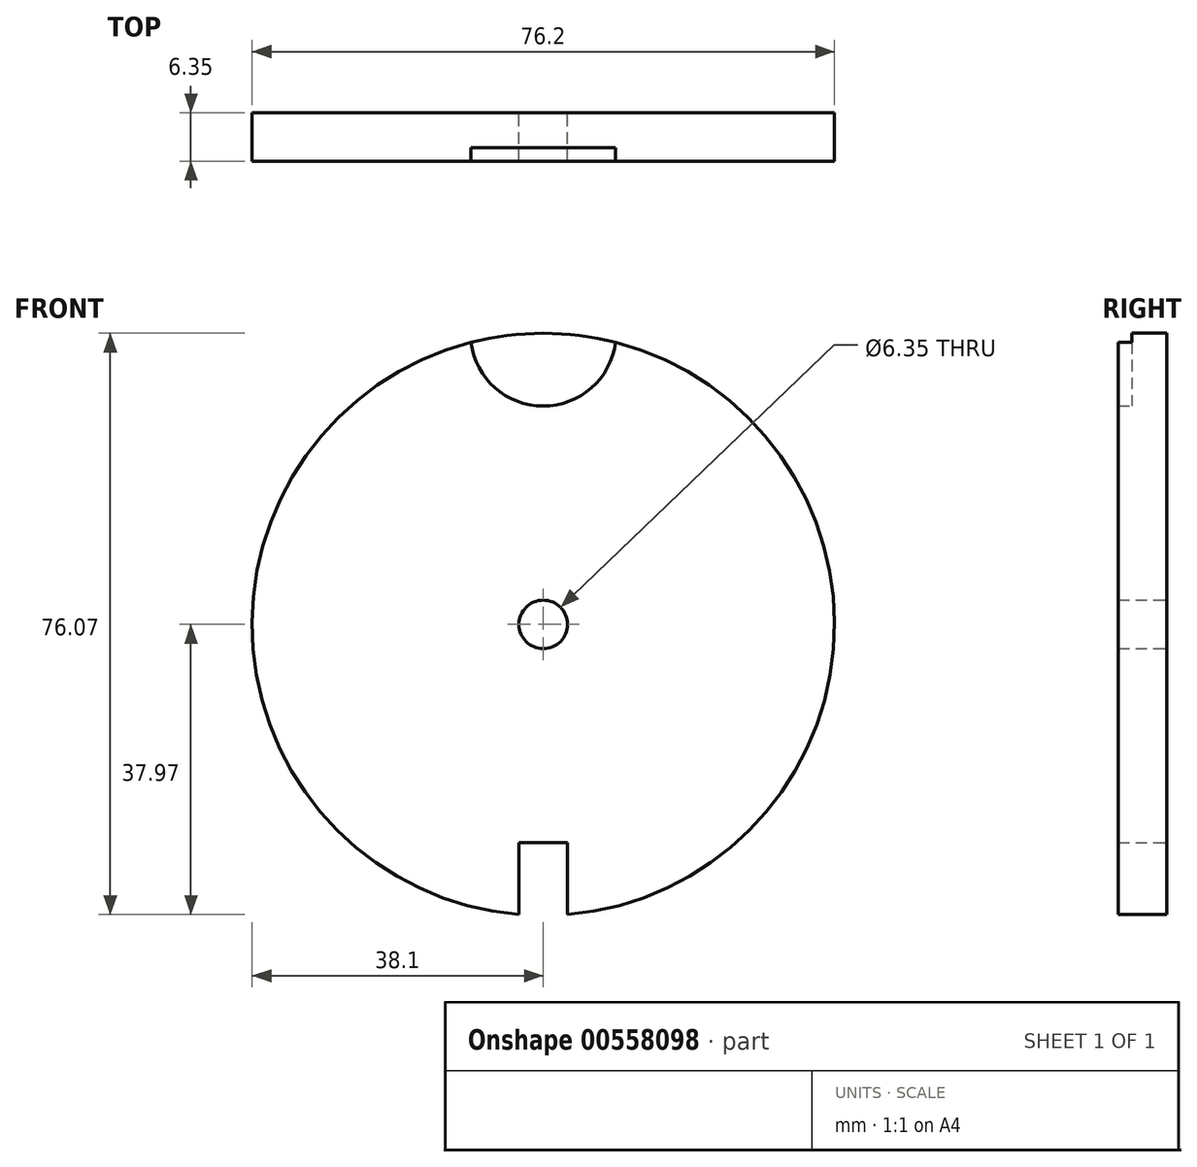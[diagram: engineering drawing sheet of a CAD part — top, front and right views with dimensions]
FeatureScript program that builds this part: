
annotation { "Feature Type Name" : "Feature", "Feature Type Description" : "" }
export const myFeature = defineFeature(function(context is Context, id is Id, definition is map)
    precondition{}
    {
        {
            var Q0;
            Q0=qCreatedBy(makeId("Front.planeOp"),FACE);
            var sketch = newSketch(context, id + "F0", { "sketchPlane" : qUnion([Q0])});
            skArc(sketch, "E0", {"start": v(-9.45, 36.9) * mm, "mid": v(-37.97, -3.18) * mm, "end": v(-3.17, -37.97) * mm});
            skCircle(sketch, "E1", {"center": v(0, 0) * mm, "radius": 3.18 * mm});
            skArc(sketch, "E2", {"start": v(-9.45, 36.9) * mm, "mid": v(0, 28.57) * mm, "end": v(9.45, 36.9) * mm});
            skLineSegment(sketch, "E3.bottom", {"start": v(3.18, -28.57) * mm, "end": v(-3.17, -28.57) * mm});
            skLineSegment(sketch, "E3.left", {"start": v(3.18, -28.57) * mm, "end": v(3.18, -37.97) * mm});
            skLineSegment(sketch, "E3.right", {"start": v(-3.17, -28.57) * mm, "end": v(-3.18, -37.97) * mm});
            skPoint(sketch, "E3.middle", {"position": v(0, -38.1) * mm});
            skArc(sketch, "E4.trimOffspring", {"start": v(3.18, -37.97) * mm, "mid": v(37.97, -3.18) * mm, "end": v(9.45, 36.9) * mm});
            skPoint(sketch, "E5.orphan", {"position": v(-3.18, -47.62) * mm});
            skPoint(sketch, "E6.orphan", {"position": v(3.18, -47.62) * mm});
            skSolve(sketch);
        }
        {
            var Q0;
            Q0 = qSketchRegion(id + "F0", true);
            extrude(context, id + "F1", {"entities" : qUnion([Q0]), "depth" : 1.78 * mm, "offsetDistance" : 25.4 * mm});
        }
        {
            var Q0;
            Q0=qCreatedBy(makeId("Front.planeOp"),FACE);
            var sketch = newSketch(context, id + "F2", { "sketchPlane" : qUnion([Q0])});
            skArc(sketch, "E7", {"start": v(3.18, -37.97) * mm, "mid": v(0, 38.1) * mm, "end": v(-3.17, -37.97) * mm});
            skCircle(sketch, "E8", {"center": v(0, 0) * mm, "radius": 3.18 * mm});
            skLineSegment(sketch, "E9.bottom", {"start": v(-3.17, -28.57) * mm, "end": v(3.18, -28.57) * mm});
            skLineSegment(sketch, "E9.left", {"start": v(-3.17, -28.57) * mm, "end": v(-3.17, -37.97) * mm});
            skLineSegment(sketch, "E9.right", {"start": v(3.18, -28.57) * mm, "end": v(3.18, -37.97) * mm});
            skPoint(sketch, "E9.middle", {"position": v(0, -38.1) * mm});
            skPoint(sketch, "E10.orphan", {"position": v(-3.17, -47.62) * mm});
            skPoint(sketch, "E11.orphan", {"position": v(3.18, -47.62) * mm});
            skSolve(sketch);
        }
        {
            var Q0;
            Q0 = qSketchRegion(id + "F2", true);
            extrude(context, id + "F3", {"entities" : qUnion([Q0]), "operationType" : NewBodyOperationType.ADD, "oppositeDirection" : true, "depth" : 4.57 * mm, "offsetDistance" : 25.4 * mm});
        }
    });
